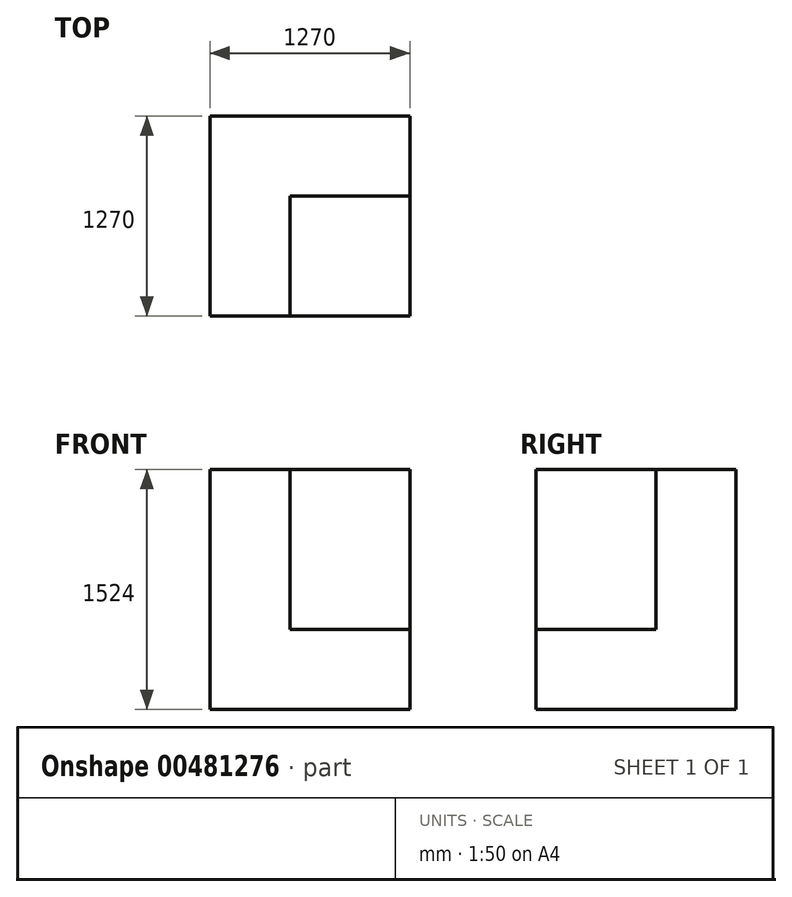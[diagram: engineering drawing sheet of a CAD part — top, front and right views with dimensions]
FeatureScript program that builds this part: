
annotation { "Feature Type Name" : "Feature", "Feature Type Description" : "" }
export const myFeature = defineFeature(function(context is Context, id is Id, definition is map)
    precondition{}
    {
        {
            var Q0;
            Q0=qCreatedBy(makeId("Front.planeOp"),FACE);
            var sketch = newSketch(context, id + "F0", { "sketchPlane" : qUnion([Q0])});
            skLineSegment(sketch, "E0", {"start": v(0, 0) * mm, "end": v(1270, 0) * mm});
            skLineSegment(sketch, "E1", {"start": v(1270, 0) * mm, "end": v(1270, 508) * mm});
            skLineSegment(sketch, "E2", {"start": v(1270, 508) * mm, "end": v(508, 508) * mm});
            skLineSegment(sketch, "E3", {"start": v(508, 508) * mm, "end": v(508, 1524) * mm});
            skLineSegment(sketch, "E4", {"start": v(508, 1524) * mm, "end": v(0, 1524) * mm});
            skLineSegment(sketch, "E5", {"start": v(0, 1524) * mm, "end": v(0, 0) * mm});
            skSolve(sketch);
        }
        {
            var Q0;
            Q0=makeQuery(id+"F0.imprint","IMPRINT",FACE,{"disambiguationData":[TD([[makeQuery(id+"F0.imprint","IMPRINT",EDGE,{"derivedFrom":sQuery(id+"F0.wireOp",EDGE,"E0")}),1.0]])]});
            extrude(context, id + "F1", {"entities" : qUnion([Q0]), "depth" : 1270 * mm});
        }
        {
            var Q0;
            Q0=makeQuery(id+"F1.opExtrude","CAP_FACE",FACE,{"disambiguationData":[OSD([sQuery(id+"F0.wireOp",EDGE,"E0"),sQuery(id+"F0.wireOp",EDGE,"E1"),sQuery(id+"F0.wireOp",EDGE,"E2"),sQuery(id+"F0.wireOp",EDGE,"E3"),sQuery(id+"F0.wireOp",EDGE,"E4"),sQuery(id+"F0.wireOp",EDGE,"E5")])],"isStart":true});
            var sketch = newSketch(context, id + "F2", { "sketchPlane" : qUnion([Q0])});
            skLineSegment(sketch, "E6", {"start": v(-508, 508) * mm, "end": v(-1270, 508) * mm});
            skLineSegment(sketch, "E7", {"start": v(-508, 508) * mm, "end": v(-508, 1524) * mm});
            skLineSegment(sketch, "E8", {"start": v(-508, 1524) * mm, "end": v(-1270, 1524) * mm});
            skLineSegment(sketch, "E9", {"start": v(-1270, 1524) * mm, "end": v(-1270, 508) * mm});
            skSolve(sketch);
        }
        {
            var Q0;
            Q0=makeQuery(id+"F2.imprint","IMPRINT",FACE,{"disambiguationData":[TD([[makeQuery(id+"F2.imprint","IMPRINT",EDGE,{"derivedFrom":sQuery(id+"F2.wireOp",EDGE,"E6")}),1.0]])]});
            extrude(context, id + "F3", {"entities" : qUnion([Q0]), "operationType" : NewBodyOperationType.ADD, "oppositeDirection" : true, "depth" : 508 * mm});
        }
    });
